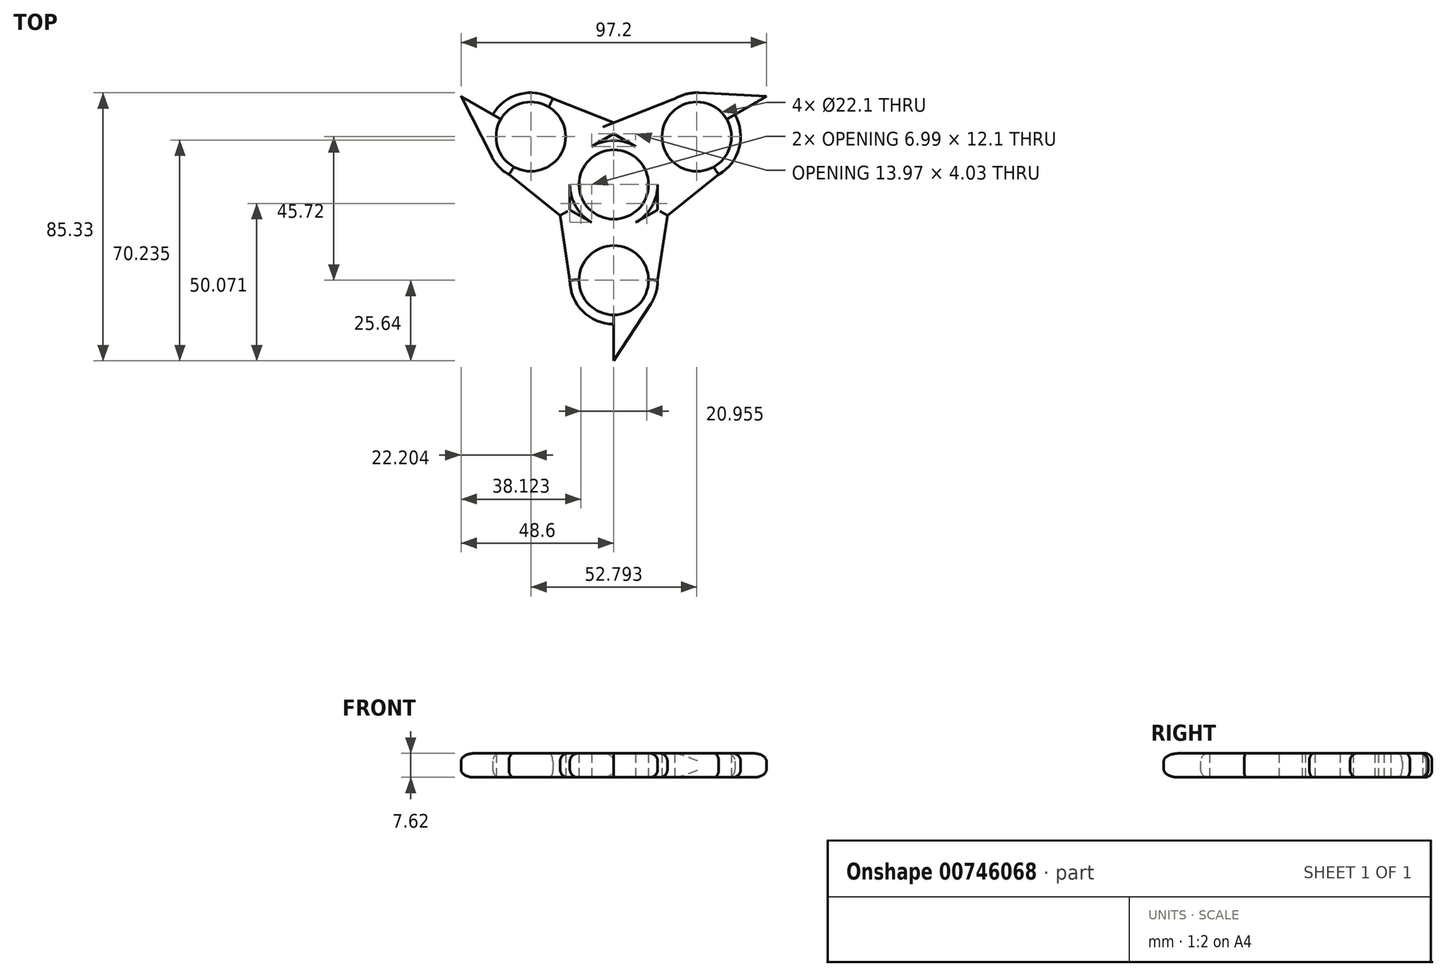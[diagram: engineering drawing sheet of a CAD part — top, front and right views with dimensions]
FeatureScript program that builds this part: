
annotation { "Feature Type Name" : "Feature", "Feature Type Description" : "" }
export const myFeature = defineFeature(function(context is Context, id is Id, definition is map)
    precondition{}
    {
        {
            var Q0;
            Q0=qCreatedBy(makeId("Top.planeOp"),FACE);
            var sketch = newSketch(context, id + "F0", { "sketchPlane" : qUnion([Q0])});
            skCircle(sketch, "E0", {"center": v(0, 0) * mm, "radius": 13.97 * mm});
            skCircle(sketch, "E1", {"center": v(-26.4, 15.24) * mm, "radius": 11.05 * mm});
            skCircle(sketch, "E2", {"center": v(0, 0) * mm, "radius": 11.05 * mm});
            skCircle(sketch, "E3", {"center": v(-26.4, 15.24) * mm, "radius": 13.97 * mm});
            skLineSegment(sketch, "E4", {"start": v(0, 0) * mm, "end": v(-26.4, 15.24) * mm});
            skCircle(sketch, "E5.1.0", {"center": v(0, -30.48) * mm, "radius": 13.97 * mm});
            skCircle(sketch, "E5.2.0", {"center": v(26.4, 15.24) * mm, "radius": 13.97 * mm});
            skCircle(sketch, "E6.1.0", {"center": v(0, -30.48) * mm, "radius": 11.05 * mm});
            skLineSegment(sketch, "E6.1.1", {"start": v(0, 0) * mm, "end": v(0, -30.48) * mm});
            skCircle(sketch, "E6.2.0", {"center": v(26.4, 15.24) * mm, "radius": 11.05 * mm});
            skLineSegment(sketch, "E6.2.1", {"start": v(0, 0) * mm, "end": v(26.4, 15.24) * mm});
            skLineSegment(sketch, "E7.bottom", {"start": v(13.97, 0) * mm, "end": v(-13.97, 0) * mm});
            skLineSegment(sketch, "E7.top", {"start": v(13.97, -30.48) * mm, "end": v(-13.97, -30.48) * mm});
            skLineSegment(sketch, "E7.left", {"start": v(13.97, 0) * mm, "end": v(13.97, -30.48) * mm});
            skLineSegment(sketch, "E7.right", {"start": v(-13.97, 0) * mm, "end": v(-13.97, -30.48) * mm});
            skPoint(sketch, "E7.middle", {"position": v(0, -15.24) * mm});
            skLineSegment(sketch, "E8.1.0", {"start": v(19.41, 27.34) * mm, "end": v(33.38, 3.14) * mm});
            skLineSegment(sketch, "E8.1.1", {"start": v(6.98, -12.1) * mm, "end": v(33.38, 3.14) * mm});
            skLineSegment(sketch, "E8.1.2", {"start": v(-6.99, 12.1) * mm, "end": v(19.41, 27.34) * mm});
            skLineSegment(sketch, "E8.1.3", {"start": v(-6.99, 12.1) * mm, "end": v(6.99, -12.1) * mm});
            skLineSegment(sketch, "E8.2.0", {"start": v(-33.38, 3.14) * mm, "end": v(-19.41, 27.34) * mm});
            skLineSegment(sketch, "E8.2.1", {"start": v(6.99, 12.1) * mm, "end": v(-19.41, 27.34) * mm});
            skLineSegment(sketch, "E8.2.2", {"start": v(-6.99, -12.1) * mm, "end": v(-33.38, 3.14) * mm});
            skLineSegment(sketch, "E8.2.3", {"start": v(-6.99, -12.1) * mm, "end": v(6.99, 12.1) * mm});
            skLineSegment(sketch, "E9", {"start": v(19.41, 27.34) * mm, "end": v(0, 19.72) * mm});
            skLineSegment(sketch, "E10", {"start": v(0, 19.72) * mm, "end": v(-19.41, 27.34) * mm});
            skLineSegment(sketch, "E11", {"start": v(0, 19.72) * mm, "end": v(19.41, 27.34) * mm});
            skLineSegment(sketch, "E12", {"start": v(26.4, 15.24) * mm, "end": v(48.6, 28.06) * mm});
            skLineSegment(sketch, "E13.1.0", {"start": v(-17.08, -9.86) * mm, "end": v(-33.38, 3.14) * mm});
            skLineSegment(sketch, "E13.1.1", {"start": v(-17.08, -9.86) * mm, "end": v(-13.97, -30.48) * mm});
            skLineSegment(sketch, "E13.2.0", {"start": v(17.08, -9.86) * mm, "end": v(13.97, -30.48) * mm});
            skLineSegment(sketch, "E13.2.1", {"start": v(17.08, -9.86) * mm, "end": v(33.38, 3.14) * mm});
            skLineSegment(sketch, "E14.1.0", {"start": v(-26.4, 15.24) * mm, "end": v(-48.6, 28.06) * mm});
            skLineSegment(sketch, "E14.2.0", {"start": v(0, -30.48) * mm, "end": v(0, -56.12) * mm});
            skLineSegment(sketch, "E15", {"start": v(-48.6, 28.06) * mm, "end": v(-38.85, 8.9) * mm});
            skLineSegment(sketch, "E16.1.0", {"start": v(0, -56.12) * mm, "end": v(11.71, -38.1) * mm});
            skLineSegment(sketch, "E16.2.0", {"start": v(48.6, 28.06) * mm, "end": v(27.13, 29.2) * mm});
            skSolve(sketch);
        }
        {
            var Q0;
            Q0 = qSketchRegion(id + "F0", true);
            var Q1;
            {var subQ1=sQuery(id+"F0.wireOp",EDGE,"E0");var subQ7=makeQuery(id+"F0.imprint","INTERSECT",VERTEX,{"derivedFrom":[subQ1,sQuery(id+"F0.wireOp",EDGE,"2a81f7ea-dfaa-4220-9730-6b88422f781c.2.0")]});Q1=makeQuery(id+"F0.imprint","IMPRINT",FACE,{"disambiguationData":[TD([[makeQuery(id+"F0.imprint","IMPRINT",EDGE,{"disambiguationData":[TD([[subQ7,-1.0]])],"derivedFrom":subQ1}),1.0]])]});}
            var Q2;
            {var subQ3=sQuery(id+"F0.wireOp",EDGE,"E4");var subQ5=sQuery(id+"F0.wireOp",EDGE,"E2");var subQ6=makeQuery(id+"F0.imprint","INTERSECT",VERTEX,{"derivedFrom":[subQ5,subQ3]});Q2=makeQuery(id+"F0.imprint","IMPRINT",FACE,{"disambiguationData":[TD([[makeQuery(id+"F0.imprint","IMPRINT",EDGE,{"disambiguationData":[TD([[subQ6,-1.0]])],"derivedFrom":subQ5}),-1.0]])]});}
            var Q3;
            {var subQ5=sQuery(id+"F0.wireOp",EDGE,"E0");var subQ8=makeQuery(id+"F0.imprint","INTERSECT",VERTEX,{"derivedFrom":[subQ5,sQuery(id+"F0.wireOp",EDGE,"ad422b94-503c-4b8c-a564-e47813131238.2.1")]});Q3=makeQuery(id+"F0.imprint","IMPRINT",FACE,{"disambiguationData":[TD([[makeQuery(id+"F0.imprint","IMPRINT",EDGE,{"disambiguationData":[TD([[subQ8,1.0]])],"derivedFrom":subQ5}),1.0]])]});}
            var Q4;
            {var subQ3=sQuery(id+"F0.wireOp",EDGE,"KG0W6A2v-qbmV-kile-noT2-Lh5GOKsosSiX");var subQ5=sQuery(id+"F0.wireOp",EDGE,"E2");var subQ6=makeQuery(id+"F0.imprint","INTERSECT",VERTEX,{"derivedFrom":[subQ5,subQ3]});Q4=makeQuery(id+"F0.imprint","IMPRINT",FACE,{"disambiguationData":[TD([[makeQuery(id+"F0.imprint","IMPRINT",EDGE,{"disambiguationData":[TD([[subQ6,1.0]])],"derivedFrom":subQ5}),-1.0]])]});}
            var Q5;
            {var subQ1=sQuery(id+"F0.wireOp",EDGE,"E0");var subQ7=makeQuery(id+"F0.imprint","INTERSECT",VERTEX,{"derivedFrom":[subQ1,sQuery(id+"F0.wireOp",EDGE,"ad422b94-503c-4b8c-a564-e47813131238.1.1")]});Q5=makeQuery(id+"F0.imprint","IMPRINT",FACE,{"disambiguationData":[TD([[makeQuery(id+"F0.imprint","IMPRINT",EDGE,{"disambiguationData":[TD([[subQ7,1.0]])],"derivedFrom":subQ1}),1.0]])]});}
            extrude(context, id + "F1", {"entities" : qUnion([Q0, Q1, Q2, Q3, Q4, Q5]), "depth" : 7.62 * mm, "offsetDistance" : 25.4 * mm});
        }
        {
            var Q0;
            Q0=makeQuery(id+"F1.opExtrude","CAP_EDGE",EDGE,{"disambiguationData":[OSD([sQuery(id+"F0.wireOp",EDGE,"E13.2.0")])],"isStart":false});
            var Q1;
            Q1=makeQuery(id+"F1.opExtrude","CAP_EDGE",EDGE,{"disambiguationData":[OSD([sQuery(id+"F0.wireOp",EDGE,"E13.2.1")])],"isStart":false});
            var Q2;
            Q2=makeQuery(id+"F1.opExtrude","CAP_EDGE",EDGE,{"disambiguationData":[OSD([sQuery(id+"F0.wireOp",EDGE,"E11")])],"isStart":false});
            var Q3;
            Q3=makeQuery(id+"F1.opExtrude","CAP_EDGE",EDGE,{"disambiguationData":[OSD([sQuery(id+"F0.wireOp",EDGE,"E10")])],"isStart":false});
            var Q4;
            Q4=makeQuery(id+"F1.opExtrude","CAP_EDGE",EDGE,{"disambiguationData":[OSD([sQuery(id+"F0.wireOp",EDGE,"E13.1.0")])],"isStart":false});
            var Q5;
            Q5=makeQuery(id+"F1.opExtrude","CAP_EDGE",EDGE,{"disambiguationData":[OSD([sQuery(id+"F0.wireOp",EDGE,"E13.1.1")])],"isStart":false});
            var Q6;
            {var subQ0=sQuery(id+"F0.wireOp",EDGE,"E5.1.0");Q6=makeQuery(id+"F1.opExtrude","CAP_EDGE",EDGE,{"disambiguationData":[OSD([subQ0]),TDD([makeQuery(id+"F0.imprint","IMPRINT",EDGE,{"disambiguationData":[TD([[makeQuery(id+"F0.imprint","INTERSECT",VERTEX,{"derivedFrom":[subQ0,sQuery(id+"F0.wireOp",EDGE,"E14.2.0")]}),1.0]])],"derivedFrom":subQ0})])],"isStart":false});}
            var Q7;
            {var subQ0=sQuery(id+"F0.wireOp",EDGE,"E5.1.0");Q7=makeQuery(id+"F1.opExtrude","CAP_EDGE",EDGE,{"disambiguationData":[OSD([subQ0]),TDD([makeQuery(id+"F0.imprint","IMPRINT",EDGE,{"disambiguationData":[TD([[makeQuery(id+"F0.imprint","INTERSECT",VERTEX,{"derivedFrom":[subQ0,sQuery(id+"F0.wireOp",EDGE,"E16.1.0")]}),-1.0]])],"derivedFrom":subQ0})])],"isStart":false});}
            var Q8;
            {var subQ0=sQuery(id+"F0.wireOp",EDGE,"E5.2.0");Q8=makeQuery(id+"F1.opExtrude","CAP_EDGE",EDGE,{"disambiguationData":[OSD([subQ0]),TDD([makeQuery(id+"F0.imprint","IMPRINT",EDGE,{"disambiguationData":[TD([[makeQuery(id+"F0.imprint","INTERSECT",VERTEX,{"derivedFrom":[subQ0,sQuery(id+"F0.wireOp",EDGE,"E12")]}),1.0]])],"derivedFrom":subQ0})])],"isStart":false});}
            var Q9;
            {var subQ0=sQuery(id+"F0.wireOp",EDGE,"E5.2.0");Q9=makeQuery(id+"F1.opExtrude","CAP_EDGE",EDGE,{"disambiguationData":[OSD([subQ0]),TDD([makeQuery(id+"F0.imprint","IMPRINT",EDGE,{"disambiguationData":[TD([[makeQuery(id+"F0.imprint","INTERSECT",VERTEX,{"derivedFrom":[subQ0,sQuery(id+"F0.wireOp",EDGE,"E16.2.0")]}),-1.0]])],"derivedFrom":subQ0})])],"isStart":false});}
            var Q10;
            {var subQ0=sQuery(id+"F0.wireOp",EDGE,"E3");Q10=makeQuery(id+"F1.opExtrude","CAP_EDGE",EDGE,{"disambiguationData":[OSD([subQ0]),TDD([makeQuery(id+"F0.imprint","IMPRINT",EDGE,{"disambiguationData":[TD([[makeQuery(id+"F0.imprint","INTERSECT",VERTEX,{"derivedFrom":[subQ0,sQuery(id+"F0.wireOp",EDGE,"E14.1.0")]}),1.0]])],"derivedFrom":subQ0})])],"isStart":false});}
            var Q11;
            {var subQ0=sQuery(id+"F0.wireOp",EDGE,"E3");Q11=makeQuery(id+"F1.opExtrude","CAP_EDGE",EDGE,{"disambiguationData":[OSD([subQ0]),TDD([makeQuery(id+"F0.imprint","IMPRINT",EDGE,{"disambiguationData":[TD([[makeQuery(id+"F0.imprint","INTERSECT",VERTEX,{"derivedFrom":[subQ0,sQuery(id+"F0.wireOp",EDGE,"E15")]}),-1.0]])],"derivedFrom":subQ0})])],"isStart":false});}
            var Q12;
            Q12=makeQuery(id+"F1.opExtrude","CAP_EDGE",EDGE,{"disambiguationData":[OSD([sQuery(id+"F0.wireOp",EDGE,"E11")])],"isStart":true});
            var Q13;
            Q13=makeQuery(id+"F1.opExtrude","CAP_EDGE",EDGE,{"disambiguationData":[OSD([sQuery(id+"F0.wireOp",EDGE,"E10")])],"isStart":true});
            var Q14;
            {var subQ0=sQuery(id+"F0.wireOp",EDGE,"E3");Q14=makeQuery(id+"F1.opExtrude","CAP_EDGE",EDGE,{"disambiguationData":[OSD([subQ0]),TDD([makeQuery(id+"F0.imprint","IMPRINT",EDGE,{"disambiguationData":[TD([[makeQuery(id+"F0.imprint","INTERSECT",VERTEX,{"derivedFrom":[subQ0,sQuery(id+"F0.wireOp",EDGE,"E14.1.0")]}),1.0]])],"derivedFrom":subQ0})])],"isStart":true});}
            var Q15;
            {var subQ0=sQuery(id+"F0.wireOp",EDGE,"E3");Q15=makeQuery(id+"F1.opExtrude","CAP_EDGE",EDGE,{"disambiguationData":[OSD([subQ0]),TDD([makeQuery(id+"F0.imprint","IMPRINT",EDGE,{"disambiguationData":[TD([[makeQuery(id+"F0.imprint","INTERSECT",VERTEX,{"derivedFrom":[subQ0,sQuery(id+"F0.wireOp",EDGE,"E15")]}),-1.0]])],"derivedFrom":subQ0})])],"isStart":true});}
            var Q16;
            Q16=makeQuery(id+"F1.opExtrude","CAP_EDGE",EDGE,{"disambiguationData":[OSD([sQuery(id+"F0.wireOp",EDGE,"E13.1.0")])],"isStart":true});
            var Q17;
            Q17=makeQuery(id+"F1.opExtrude","CAP_EDGE",EDGE,{"disambiguationData":[OSD([sQuery(id+"F0.wireOp",EDGE,"E13.1.1")])],"isStart":true});
            var Q18;
            {var subQ0=sQuery(id+"F0.wireOp",EDGE,"E5.1.0");Q18=makeQuery(id+"F1.opExtrude","CAP_EDGE",EDGE,{"disambiguationData":[OSD([subQ0]),TDD([makeQuery(id+"F0.imprint","IMPRINT",EDGE,{"disambiguationData":[TD([[makeQuery(id+"F0.imprint","INTERSECT",VERTEX,{"derivedFrom":[subQ0,sQuery(id+"F0.wireOp",EDGE,"E14.2.0")]}),1.0]])],"derivedFrom":subQ0})])],"isStart":true});}
            var Q19;
            {var subQ0=sQuery(id+"F0.wireOp",EDGE,"E5.1.0");Q19=makeQuery(id+"F1.opExtrude","CAP_EDGE",EDGE,{"disambiguationData":[OSD([subQ0]),TDD([makeQuery(id+"F0.imprint","IMPRINT",EDGE,{"disambiguationData":[TD([[makeQuery(id+"F0.imprint","INTERSECT",VERTEX,{"derivedFrom":[subQ0,sQuery(id+"F0.wireOp",EDGE,"E16.1.0")]}),-1.0]])],"derivedFrom":subQ0})])],"isStart":true});}
            var Q20;
            Q20=makeQuery(id+"F1.opExtrude","CAP_EDGE",EDGE,{"disambiguationData":[OSD([sQuery(id+"F0.wireOp",EDGE,"E13.2.0")])],"isStart":true});
            var Q21;
            Q21=makeQuery(id+"F1.opExtrude","CAP_EDGE",EDGE,{"disambiguationData":[OSD([sQuery(id+"F0.wireOp",EDGE,"E13.2.1")])],"isStart":true});
            var Q22;
            {var subQ0=sQuery(id+"F0.wireOp",EDGE,"E5.2.0");Q22=makeQuery(id+"F1.opExtrude","CAP_EDGE",EDGE,{"disambiguationData":[OSD([subQ0]),TDD([makeQuery(id+"F0.imprint","IMPRINT",EDGE,{"disambiguationData":[TD([[makeQuery(id+"F0.imprint","INTERSECT",VERTEX,{"derivedFrom":[subQ0,sQuery(id+"F0.wireOp",EDGE,"E12")]}),1.0]])],"derivedFrom":subQ0})])],"isStart":true});}
            var Q23;
            {var subQ0=sQuery(id+"F0.wireOp",EDGE,"E5.2.0");Q23=makeQuery(id+"F1.opExtrude","CAP_EDGE",EDGE,{"disambiguationData":[OSD([subQ0]),TDD([makeQuery(id+"F0.imprint","IMPRINT",EDGE,{"disambiguationData":[TD([[makeQuery(id+"F0.imprint","INTERSECT",VERTEX,{"derivedFrom":[subQ0,sQuery(id+"F0.wireOp",EDGE,"E16.2.0")]}),-1.0]])],"derivedFrom":subQ0})])],"isStart":true});}
            fillet(context, id + "F2", {"entities" : qUnion([Q0, Q1, Q2, Q3, Q4, Q5, Q6, Q7, Q8, Q9, Q10, Q11, Q12, Q13, Q14, Q15, Q16, Q17, Q18, Q19, Q20, Q21, Q22, Q23]), "radius" : 2.54 * mm, "tangentPropagation" : true, "allowEdgeOverflow" : false});
        }
    });
